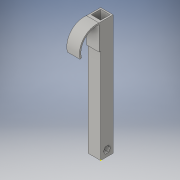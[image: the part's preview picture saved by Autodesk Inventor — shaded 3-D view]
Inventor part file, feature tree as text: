
AUTODESK INVENTOR PART (.ipt)
format: ipt  version: 2016 (Build 200138000, 138)  size: 143,872 bytes
history: native  units: in
note: dims shown in document units (in); Inventor stores cm internally (conversion verified against a paired STEP export)
features: sketch x5, extrude x4
ambient origin geometry x8: Origin, YZ Plane, XZ Plane, XY Plane, X Axis, Y Axis, Z Axis, Center Point
bodies: Solid1 (feature_tree)
feature tree (9):
  extrude  "Extrusion1"  Depth=1.0in
  extrude  "Extrusion2"  Depth=0.5in
  extrude  "Extrusion3"  Depth=0.125in
  sketch  "Sketch4"  dims[d8=9.0in d9=0.0in d11=2.0in]
  extrude  "Extrusion4"  Depth=2.0in
  sketch  "Sketch1"  dims[d0=9.5in d1=1.0in]
  sketch  "Sketch2"  dims[d3=0.5in d4=0.5in]
  sketch  "Sketch3"  dims[d5=1.0in d6=0.0in d7=0.125in]
  sketch  "Sketch5"  dims[d13=0.125in d15=0.125in d16=1.0in d17=0.0in d18=1.75in d19=1.5in d20=0.125in d21=0.125in d22=1.0in d23=0.0in]
